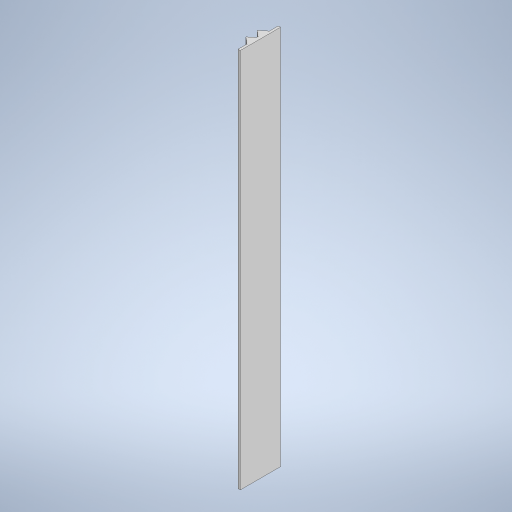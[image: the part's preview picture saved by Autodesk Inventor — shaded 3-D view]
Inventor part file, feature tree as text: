
AUTODESK INVENTOR PART (.ipt)
format: ipt  version: 2024 (Build 280153000, 153)  size: 247,808 bytes
history: native  units: mm
features: chamfer x2, extrude x1, sketch x1
ambient origin geometry x8: Origin, YZ Plane, XZ Plane, XY Plane, X Axis, Y Axis, Z Axis, Center Point
bodies: Solid1 (feature_tree)
feature tree (4):
  extrude  "Extrusion1"  Depth=2.0mm TaperAngle=45.0deg
  chamfer  "Chamfer1"  Distance=2.0mm Angle=45.0deg
  chamfer  "Chamfer2"  [1 undecoded]
  sketch  "Sketch1"  dims[d1=340.0mm d2=0.0mm d3=0.1mm d4=2.0mm d5=45.0deg d6=1.0mm d7=2.0mm d8=45.0deg]
note: 1 required parameter value undecoded (feature->parameter linkage not recoverable at this tier; creation-order binding heuristic only, values carry confidence <= 0.55)
